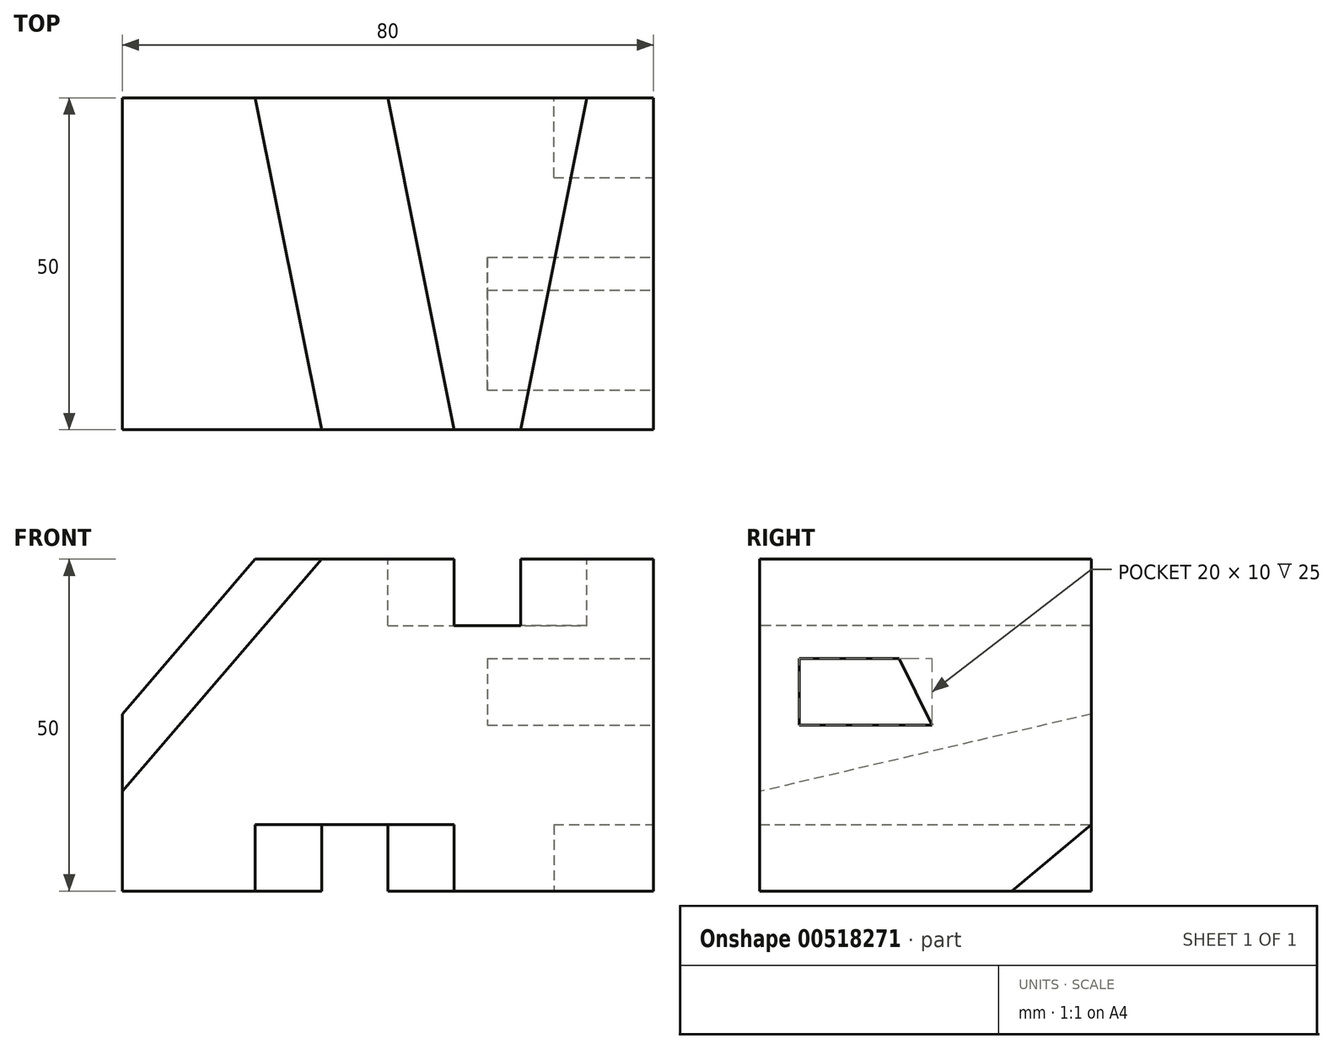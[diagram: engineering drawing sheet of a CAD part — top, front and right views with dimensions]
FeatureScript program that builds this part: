
annotation { "Feature Type Name" : "Feature", "Feature Type Description" : "" }
export const myFeature = defineFeature(function(context is Context, id is Id, definition is map)
    precondition{}
    {
        {
            var Q0;
            Q0=qCreatedBy(makeId("Top.planeOp"),FACE);
            var sketch = newSketch(context, id + "F0", { "sketchPlane" : qUnion([Q0])});
            skLineSegment(sketch, "E0.bottom", {"start": v(0, 0) * mm, "end": v(80, 0) * mm});
            skLineSegment(sketch, "E0.top", {"start": v(0, 50) * mm, "end": v(80, 50) * mm});
            skLineSegment(sketch, "E0.left", {"start": v(0, 0) * mm, "end": v(0, 50) * mm});
            skLineSegment(sketch, "E0.right", {"start": v(80, 0) * mm, "end": v(80, 50) * mm});
            skSolve(sketch);
        }
        {
            var Q0;
            Q0=makeQuery(id+"F0.imprint","IMPRINT",FACE,{"disambiguationData":[TD([[makeQuery(id+"F0.imprint","IMPRINT",EDGE,{"derivedFrom":sQuery(id+"F0.wireOp",EDGE,"E0.bottom")}),1.0]])]});
            extrude(context, id + "F1", {"entities" : qUnion([Q0]), "depth" : 50 * mm, "offsetDistance" : 25 * mm});
        }
        {
            var Q0;
            Q0=makeQuery(id+"F1.opExtrude","CAP_FACE",FACE,{"disambiguationData":[OSD([sQuery(id+"F0.wireOp",EDGE,"E0.bottom"),sQuery(id+"F0.wireOp",EDGE,"E0.top"),sQuery(id+"F0.wireOp",EDGE,"E0.left"),sQuery(id+"F0.wireOp",EDGE,"E0.right")])],"isStart":false});
            var sketch = newSketch(context, id + "F2", { "sketchPlane" : qUnion([Q0])});
            skLineSegment(sketch, "E1", {"start": v(40, 50) * mm, "end": v(50, 0) * mm});
            skLineSegment(sketch, "E2", {"start": v(70, 50) * mm, "end": v(60, 0) * mm});
            skLineSegment(sketch, "E3", {"start": v(60, 0) * mm, "end": v(50, 0) * mm});
            skSolve(sketch);
        }
        {
            var Q0;
            {var subQ0=sQuery(id+"F2.wireOp",EDGE,"E1");Q0=makeQuery(id+"F2.imprint","IMPRINT",FACE,{"disambiguationData":[TD([[makeQuery(id+"F2.imprint","IMPRINT",EDGE,{"derivedFrom":subQ0}),1.0]])]});}
            extrude(context, id + "F3", {"entities" : qUnion([Q0]), "operationType" : NewBodyOperationType.REMOVE, "oppositeDirection" : true, "depth" : 10 * mm, "offsetDistance" : 25 * mm});
        }
        {
            var Q0;
            Q0=makeQuery(id+"F1.opExtrude","CAP_FACE",FACE,{"disambiguationData":[OSD([sQuery(id+"F0.wireOp",EDGE,"E0.bottom"),sQuery(id+"F0.wireOp",EDGE,"E0.top"),sQuery(id+"F0.wireOp",EDGE,"E0.left"),sQuery(id+"F0.wireOp",EDGE,"E0.right")])],"isStart":true});
            var sketch = newSketch(context, id + "F4", { "sketchPlane" : qUnion([Q0])});
            skLineSegment(sketch, "E4", {"start": v(20, 0) * mm, "end": v(30, -50) * mm});
            skLineSegment(sketch, "E5", {"start": v(30, -50) * mm, "end": v(40, -50) * mm});
            skLineSegment(sketch, "E6", {"start": v(40, -50) * mm, "end": v(50, 0) * mm});
            skSolve(sketch);
        }
        {
            var Q0;
            {var subQ0=sQuery(id+"F4.wireOp",EDGE,"E4");Q0=makeQuery(id+"F4.imprint","IMPRINT",FACE,{"disambiguationData":[TD([[makeQuery(id+"F4.imprint","IMPRINT",EDGE,{"derivedFrom":subQ0}),1.0]])]});}
            extrude(context, id + "F5", {"entities" : qUnion([Q0]), "operationType" : NewBodyOperationType.REMOVE, "oppositeDirection" : true, "depth" : 10 * mm, "offsetDistance" : 25 * mm});
        }
        {
            var Q0;
            Q0=makeQuery(id+"F1.opExtrude","SWEPT_FACE",FACE,{"disambiguationData":[OSD([sQuery(id+"F0.wireOp",EDGE,"E0.right")])]});
            var sketch = newSketch(context, id + "F6", { "sketchPlane" : qUnion([Q0])});
            skLineSegment(sketch, "E7", {"start": v(6, 35) * mm, "end": v(6, 25) * mm});
            skLineSegment(sketch, "E8", {"start": v(6, 25) * mm, "end": v(26, 25) * mm});
            skLineSegment(sketch, "E9", {"start": v(26, 25) * mm, "end": v(21, 35) * mm});
            skLineSegment(sketch, "E10", {"start": v(21, 35) * mm, "end": v(6, 35) * mm});
            skSolve(sketch);
        }
        {
            var Q0;
            Q0=makeQuery(id+"F6.imprint","IMPRINT",FACE,{"disambiguationData":[TD([[makeQuery(id+"F6.imprint","IMPRINT",EDGE,{"derivedFrom":sQuery(id+"F6.wireOp",EDGE,"E7")}),1.0]])]});
            extrude(context, id + "F7", {"entities" : qUnion([Q0]), "operationType" : NewBodyOperationType.REMOVE, "oppositeDirection" : true, "depth" : 25 * mm, "offsetDistance" : 25 * mm});
        }
        {
            var Q0;
            Q0=makeQuery(id+"F1.opExtrude","SWEPT_FACE",FACE,{"disambiguationData":[OSD([sQuery(id+"F0.wireOp",EDGE,"E0.right")])]});
            var sketch = newSketch(context, id + "F8", { "sketchPlane" : qUnion([Q0])});
            skLineSegment(sketch, "E11", {"start": v(50, 10) * mm, "end": v(38, 0) * mm});
            skSolve(sketch);
        }
        {
            var Q0;
            {var subQ0=sQuery(id+"F8.wireOp",EDGE,"E11");Q0=makeQuery(id+"F8.imprint","IMPRINT",FACE,{"disambiguationData":[TD([[makeQuery(id+"F8.imprint","IMPRINT",EDGE,{"derivedFrom":subQ0}),1.0]])]});}
            extrude(context, id + "F9", {"entities" : qUnion([Q0]), "operationType" : NewBodyOperationType.REMOVE, "oppositeDirection" : true, "depth" : 15 * mm, "offsetDistance" : 25 * mm});
        }
        {
            var Q0;
            {var subQ0=sQuery(id+"F0.wireOp",EDGE,"E0.bottom");var subQ1=sQuery(id+"F0.wireOp",EDGE,"E0.top");var subQ2=sQuery(id+"F0.wireOp",EDGE,"E0.left");Q0=makeQuery(id+"F3.boolean.opBoolean","SPLIT",FACE,{"disambiguationData":[TD([makeQuery(id+"F1.opExtrude","SWEPT_FACE",FACE,{"disambiguationData":[OSD([subQ2])]})])],"derivedFrom":makeQuery(id+"F1.opExtrude","CAP_FACE",FACE,{"disambiguationData":[OSD([subQ0,subQ1,subQ2,sQuery(id+"F0.wireOp",EDGE,"E0.right")])],"isStart":false})});}
            var sketch = newSketch(context, id + "F10", { "sketchPlane" : qUnion([Q0])});
            skLineSegment(sketch, "E12", {"start": v(20, 50) * mm, "end": v(30, 0) * mm});
            skSolve(sketch);
        }
        {
            var Q0;
            Q0=makeQuery(id+"F1.opExtrude","SWEPT_FACE",FACE,{"disambiguationData":[OSD([sQuery(id+"F0.wireOp",EDGE,"E0.bottom")])]});
            var sketch = newSketch(context, id + "F11", { "sketchPlane" : qUnion([Q0])});
            skLineSegment(sketch, "E13", {"start": v(30, 50) * mm, "end": v(0, 15) * mm});
            skSolve(sketch);
        }
        {
            var Q0;
            {var subQ0=sQuery(id+"F11.wireOp",EDGE,"E13");Q0=makeQuery(id+"F11.imprint","IMPRINT",FACE,{"disambiguationData":[TD([[makeQuery(id+"F11.imprint","IMPRINT",EDGE,{"derivedFrom":subQ0}),-1.0]])]});}
            var Q1;
            Q1=sQuery(id+"F10.wireOp",EDGE,"E12");
            sweep(context, id + "F12", {"operationType" : NewBodyOperationType.REMOVE, "profiles" : qUnion([Q0]), "path" : qUnion([Q1])});
        }
    });
